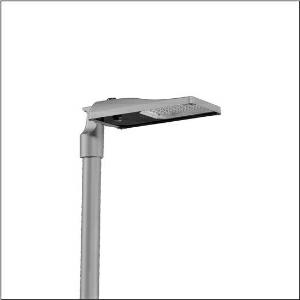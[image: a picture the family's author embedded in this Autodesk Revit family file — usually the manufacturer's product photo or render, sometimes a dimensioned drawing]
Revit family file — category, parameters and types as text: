
# Revit family: streetlight_sl_31_mini___stw1_0a_5xh6e31t08ja_04bd
name_source: partatom
category: Lighting Fixtures
units: mm (PartAtom-declared; Revit-internal decimal feet)

## family parameters
Cut with Voids When Loaded = No
Host = Face
Light Source = No
Part Type = Normal
Room Calculation Point = No
Round Connector Dimension = Use Diameter
Shared = No

## types (1)
- --- (1 x LED, 12270 lm, 82.5 W, 3000K)
    Apparent Load = 83 VA
    CIE Flux Codes = 39 75 98 100 100
    Color Rendering = 70
    Color Temperature = 3000K
    Default Elevation = 1800 mm
    Description = Streetlight SL 31 mini D4i, Desk-Remote mast luminaire for post-top, side-entry; light control with lens of PMMA; light distribution: STW1.0a, direct asymmetric distribution, for standard-compliant lighting for roads and squares; LED: luminous flux: 12.270lm, light colour: 730, colour temperature: 3000K; luminous efficacy: 148,7lm/W; control: pre-setting: logarithmic dimming characteristic, flexible luminous flux parameterisation, time-dependent luminous flux control, constant luminous flux control, power reduction, intelligent temperature release in ECG and LED module, overheat protection; luminaire housing, of diecast aluminium, Siteco® metallic grey (DB 702S), corrosivity category C5 high according to DIN EN ISO 12944; cover of toughened safety glass, transparent, opened without tools; mast flange of diecast aluminium, Siteco® metallic grey (DB 702S), spigot size: 76/60mm, mast flange included unmounted; with cable H07RN-F 2x 1.5mm², cable length: 10,5m, connection cable pre-assembled; mains connection: 220..240V, AC, 50/60Hz; power consumption (at start of service life): 82,5W / (at end of service life): 90,1W / (with reduced operation 50%): 36,8W; protection rating (complete): IP66; insulation class (complete): insulation class II (safety insulation); impact resistance: IK09; certification: CE, ENEC, ENEC+, VDE, UKCA, ZD4i; permissible operating ambient temperature for outdoor applications: -40..+50°C; packaging unit: 1 piece

Light Distribution: STW1.0a
    Height = 76 mm
    Lamp = 1 x LED
    Lamp Light Flux = 12270 lm
    Lamp Power = 82.5 W
    Lamp count = 1
    Length = 547 mm
    Luminous efficacy = 149 lm/W
    Manufacturer = Siteco
    ModVariant = No
    Model = 5XH6E31T08JA
    Number of Poles = 1
    OnlyDefault = Yes
    Power Factor = 1
    Product Name = Streetlight SL 31 mini | STW1.0a
    Product group = mast luminaire | pylon top
    ProductGroupID = 6100
    Protection Class = Protection class II
    Protection Degree = IP 66
    RLX_Detail_Level = 1
    RLX_Emergency_Light_Flux = 0 lm
    RLX_Emergency_Type = 0
    RLX_Emergency_Type_DB = No
    RlxData = <blob elided: 40093 chars, md5=be20be25>
    Socket = socket
    Standby Power = 0 W
    System Light Flux = 12270 lm
    System Power = 83 W
    Type Comments = factory setting: luminous flux: 100 % | dim-lin: 254 | 870 mA
    Type Image = l_1300332.jpg
    URL = http://relux.com
    VarID = @adj_046774
    Voltage = 0 V
    Weight = 0.00 kg
    Width = 265 mm

## geometry (parser evidence)
native form markers: Blend x4, Sweep x11
no freeform markers — native parametric forms only
